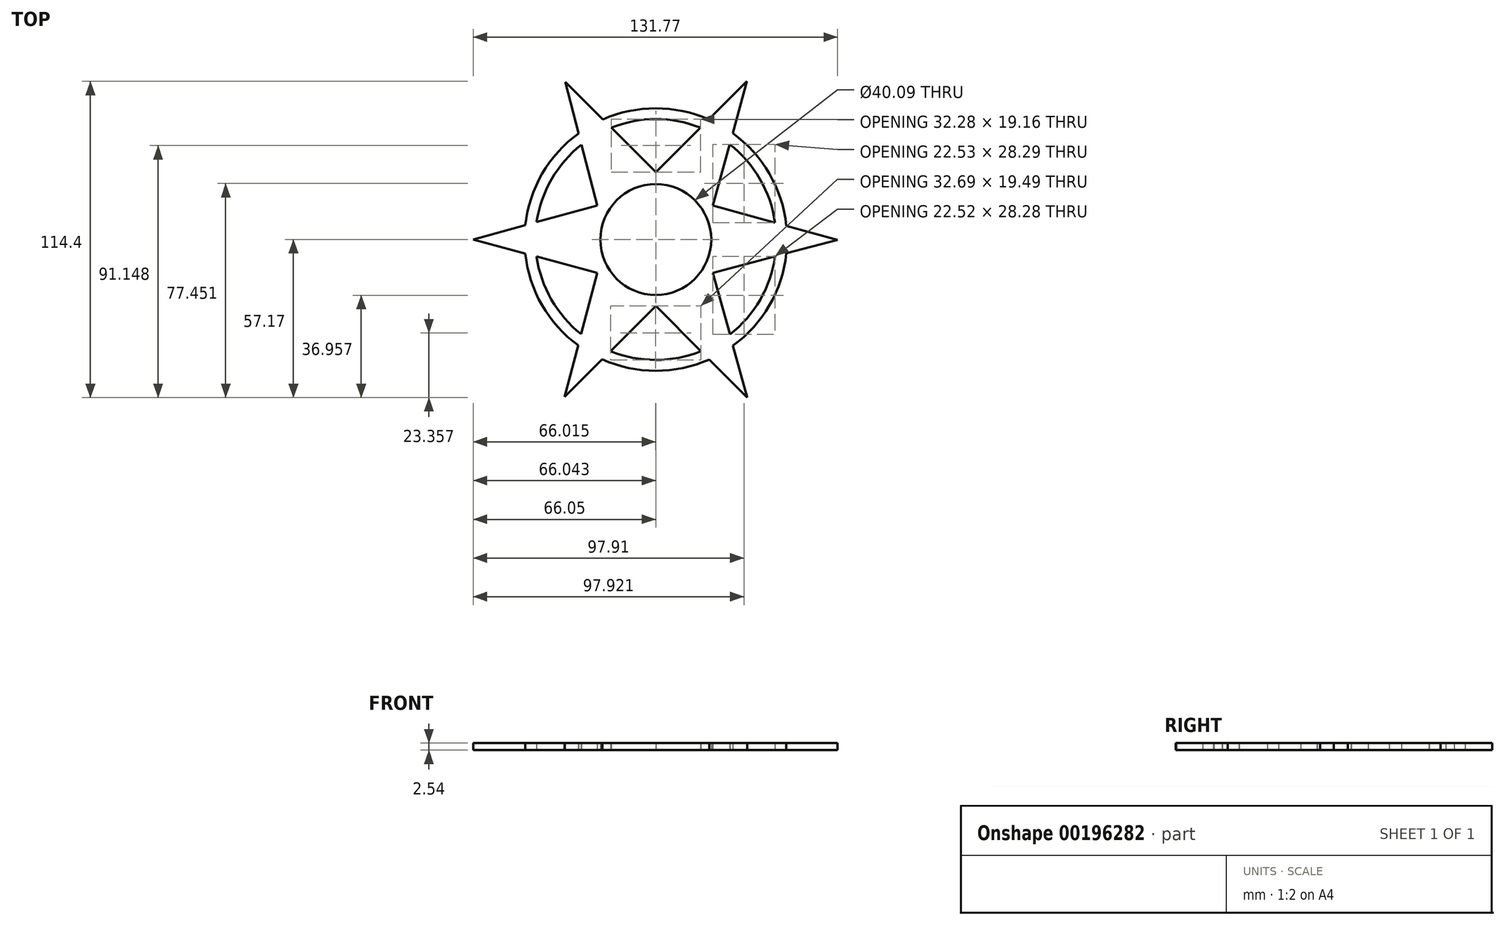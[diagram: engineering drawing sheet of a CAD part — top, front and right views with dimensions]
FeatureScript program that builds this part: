
annotation { "Feature Type Name" : "Feature", "Feature Type Description" : "" }
export const myFeature = defineFeature(function(context is Context, id is Id, definition is map)
    precondition{}
    {
        {
            var Q0;
            Q0=qCreatedBy(makeId("Top.planeOp"),FACE);
            var sketch = newSketch(context, id + "F0", { "sketchPlane" : qUnion([Q0])});
            skLineSegment(sketch, "E0.1", {"start": v(-13.8, -24.05) * mm, "end": v(-14.34, -24.05) * mm});
            skPoint(sketch, "E0.0.midPoint", {"position": v(20.61, -12) * mm});
            skPoint(sketch, "E1.center", {"position": v(0, 0) * mm});
            skCircle(sketch, "E2", {"center": v(0, 0) * mm, "radius": 20.05 * mm});
            skCircle(sketch, "E3", {"center": v(0, 0) * mm, "radius": 15.26 * mm});
            skCircle(sketch, "E4", {"center": v(0, 0) * mm, "radius": 13.55 * mm});
            skCircle(sketch, "E5", {"center": v(0, 0) * mm, "radius": 3 * mm});
            skPoint(sketch, "E6", {"position": v(0, 24.4) * mm});
            skPoint(sketch, "E7", {"position": v(0, -24.07) * mm});
            skPoint(sketch, "E8", {"position": v(-21.15, 12.36) * mm});
            skPoint(sketch, "E9", {"position": v(20.6, 12.36) * mm});
            skPoint(sketch, "E10", {"position": v(-21.17, -12) * mm});
            skPoint(sketch, "E11", {"position": v(-32.76, 56.98) * mm});
            skLineSegment(sketch, "E12", {"start": v(0, 24.4) * mm, "end": v(16.13, 40.46) * mm});
            skLineSegment(sketch, "E13", {"start": v(20.6, 12.36) * mm, "end": v(32.97, 57.23) * mm});
            skLineSegment(sketch, "E14", {"start": v(20.6, 12.36) * mm, "end": v(43.12, 6.13) * mm});
            skLineSegment(sketch, "E15", {"start": v(20.61, -12) * mm, "end": v(43.13, -6.07) * mm});
            skLineSegment(sketch, "E16", {"start": v(20.61, -12) * mm, "end": v(26.78, -34.35) * mm});
            skLineSegment(sketch, "E17", {"start": v(0, -24.07) * mm, "end": v(16.3, -40.39) * mm});
            skLineSegment(sketch, "E18", {"start": v(-32.96, -56.86) * mm, "end": v(-19.38, -43.35) * mm});
            skLineSegment(sketch, "E19", {"start": v(-32.96, -56.86) * mm, "end": v(-28.08, -38.29) * mm});
            skLineSegment(sketch, "E20", {"start": v(-21.17, -12) * mm, "end": v(-43.12, -6.16) * mm});
            skLineSegment(sketch, "E21", {"start": v(-66.05, -0.06) * mm, "end": v(-47.2, 5.16) * mm});
            skLineSegment(sketch, "E22", {"start": v(-21.15, 12.36) * mm, "end": v(-26.86, 34.3) * mm});
            skLineSegment(sketch, "E23", {"start": v(-32.76, 56.98) * mm, "end": v(-19.15, 43.45) * mm});
            skArc(sketch, "E24", {"start": v(16.13, 40.46) * mm, "mid": v(0, 43.56) * mm, "end": v(-16.15, 40.45) * mm});
            skArc(sketch, "E25", {"start": v(19.14, 43.45) * mm, "mid": v(0, 47.48) * mm, "end": v(-19.15, 43.45) * mm});
            skLineSegment(sketch, "E26.trimOffspring", {"start": v(-16.15, 40.45) * mm, "end": v(0, 24.4) * mm});
            skLineSegment(sketch, "E27.trimOffspring", {"start": v(-27.93, 38.4) * mm, "end": v(-32.76, 56.98) * mm});
            skLineSegment(sketch, "E28.trimOffspring", {"start": v(19.14, 43.45) * mm, "end": v(32.97, 57.23) * mm});
            skArc(sketch, "E29.trimOffspring", {"start": v(-27.93, 38.4) * mm, "mid": v(-41.08, 23.81) * mm, "end": v(-47.2, 5.16) * mm});
            skArc(sketch, "E30.trimOffspring", {"start": v(-26.86, 34.3) * mm, "mid": v(-37.68, 21.86) * mm, "end": v(-43.1, 6.3) * mm});
            skLineSegment(sketch, "E31.trimOffspring", {"start": v(-14.2, 24.45) * mm, "end": v(-14.18, 24.47) * mm});
            skArc(sketch, "E32.trimOffspring", {"start": v(47.22, 5) * mm, "mid": v(41.08, 23.81) * mm, "end": v(27.8, 38.49) * mm});
            skArc(sketch, "E33.trimOffspring", {"start": v(43.12, 6.13) * mm, "mid": v(37.66, 21.88) * mm, "end": v(26.68, 34.43) * mm});
            skLineSegment(sketch, "E34.trimOffspring", {"start": v(47.22, 5) * mm, "end": v(65.72, -0.12) * mm});
            skLineSegment(sketch, "E35.trimOffspring", {"start": v(47.22, -5) * mm, "end": v(65.72, -0.12) * mm});
            skPoint(sketch, "E36.orphan", {"position": v(27.62, 0.07) * mm});
            skPoint(sketch, "E37.orphan", {"position": v(13.6, -24.09) * mm});
            skPoint(sketch, "E38.orphan", {"position": v(14.2, -24.08) * mm});
            skArc(sketch, "E39.trimOffspring", {"start": v(26.78, -34.35) * mm, "mid": v(37.7, -21.8) * mm, "end": v(43.13, -6.07) * mm});
            skArc(sketch, "E40.trimOffspring", {"start": v(27.9, -38.42) * mm, "mid": v(41.1, -23.76) * mm, "end": v(47.22, -5) * mm});
            skLineSegment(sketch, "E41.trimOffspring", {"start": v(27.9, -38.42) * mm, "end": v(33.08, -57.17) * mm});
            skLineSegment(sketch, "E42.trimOffspring", {"start": v(19.3, -43.38) * mm, "end": v(33.08, -57.17) * mm});
            skArc(sketch, "E43.trimOffspring", {"start": v(-16.38, -40.36) * mm, "mid": v(-0.04, -43.56) * mm, "end": v(16.3, -40.39) * mm});
            skLineSegment(sketch, "E44.trimOffspring", {"start": v(-27, -34.18) * mm, "end": v(-21.17, -12) * mm});
            skArc(sketch, "E45.trimOffspring", {"start": v(-19.38, -43.35) * mm, "mid": v(-0.04, -47.48) * mm, "end": v(19.3, -43.38) * mm});
            skLineSegment(sketch, "E46.trimOffspring", {"start": v(-16.38, -40.36) * mm, "end": v(0, -24.07) * mm});
            skPoint(sketch, "E47.orphan", {"position": v(-27.95, -0.25) * mm});
            skArc(sketch, "E48.trimOffspring", {"start": v(-47.2, -5.07) * mm, "mid": v(-41.14, -23.7) * mm, "end": v(-28.08, -38.29) * mm});
            skPoint(sketch, "E0.3.start.orphan", {"position": v(-28.12, 0.26) * mm});
            skArc(sketch, "E49.trimOffspring", {"start": v(-43.12, -6.16) * mm, "mid": v(-37.75, -21.72) * mm, "end": v(-27, -34.18) * mm});
            skLineSegment(sketch, "E50.trimOffspring", {"start": v(-43.1, 6.3) * mm, "end": v(-21.15, 12.36) * mm});
            skLineSegment(sketch, "E51.trimOffspring", {"start": v(-47.2, -5.07) * mm, "end": v(-66.05, -0.06) * mm});
            skSolve(sketch);
        }
        {
            var Q0;
            Q0=makeQuery(id+"F0.imprint","IMPRINT",FACE,{"disambiguationData":[TD([[makeQuery(id+"F0.imprint","IMPRINT",EDGE,{"derivedFrom":sQuery(id+"F0.wireOp",EDGE,"E2")}),-1.0]])]});
            extrude(context, id + "F1", {"entities" : qUnion([Q0]), "depth" : 2.54 * mm});
        }
    });
